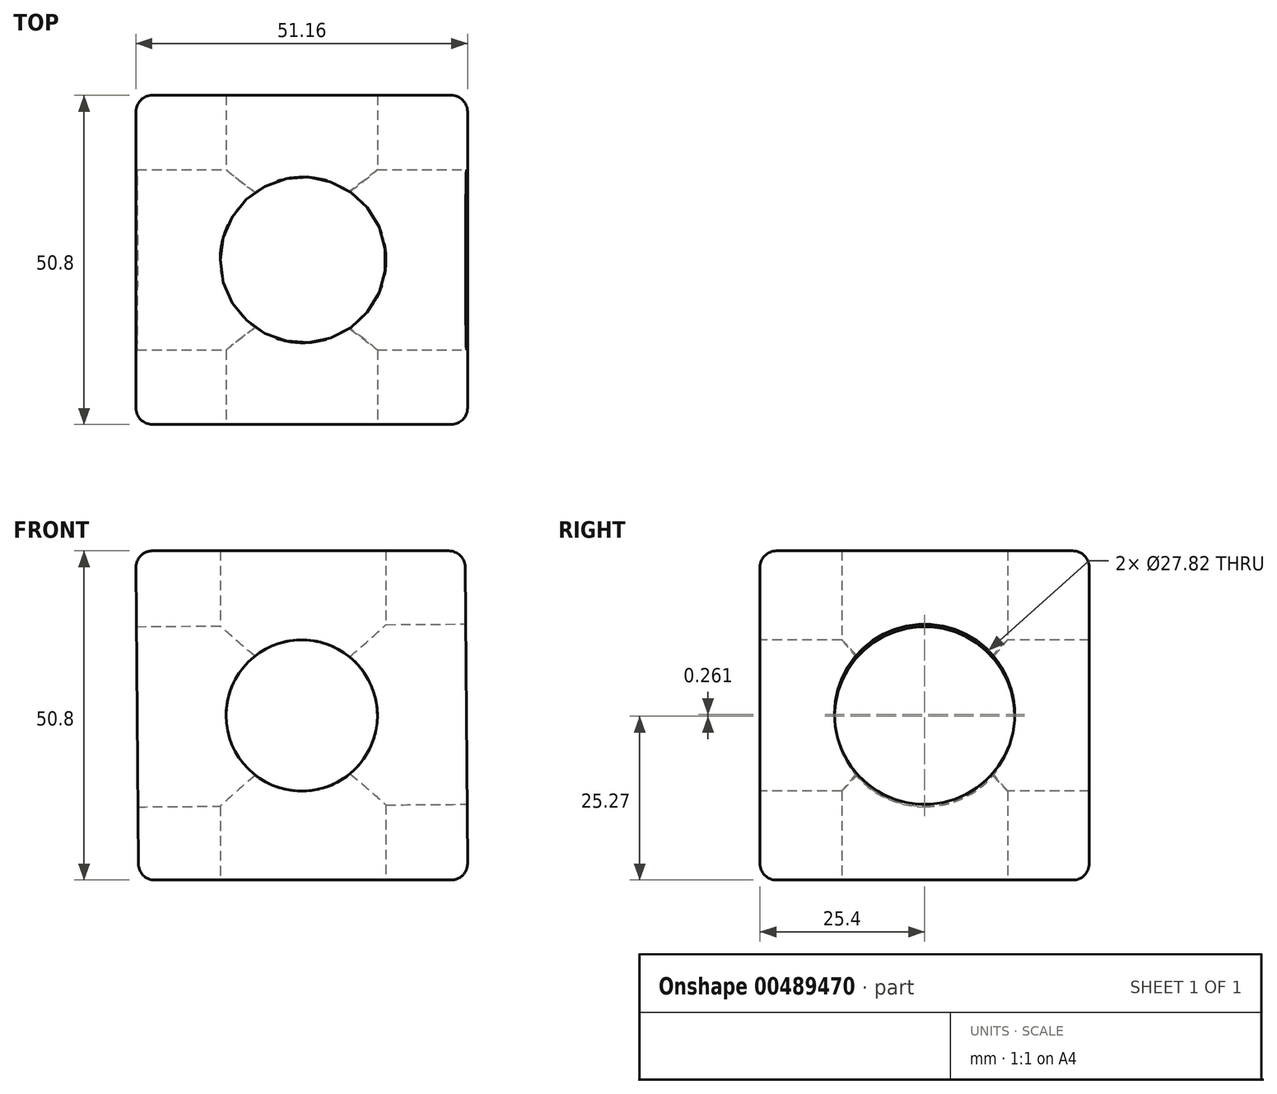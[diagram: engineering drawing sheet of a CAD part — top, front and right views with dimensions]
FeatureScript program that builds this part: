
annotation { "Feature Type Name" : "Feature", "Feature Type Description" : "" }
export const myFeature = defineFeature(function(context is Context, id is Id, definition is map)
    precondition{}
    {
        {
            var Q0;
            Q0=qCreatedBy(makeId("Front.planeOp"),FACE);
            var sketch = newSketch(context, id + "F0", { "sketchPlane" : qUnion([Q0])});
            skLineSegment(sketch, "E0", {"start": v(50.8, 0) * mm, "end": v(50.4, 50.8) * mm});
            skLineSegment(sketch, "E1", {"start": v(50.4, 50.8) * mm, "end": v(-0.4, 50.8) * mm});
            skLineSegment(sketch, "E2", {"start": v(0, 0) * mm, "end": v(50.8, 0) * mm});
            skLineSegment(sketch, "E3", {"start": v(-0.4, 50.8) * mm, "end": v(0, 0) * mm});
            skSolve(sketch);
        }
        {
            var Q0;
            Q0 = qSketchRegion(id + "F0", true);
            extrude(context, id + "F1", {"entities" : qUnion([Q0]), "depth" : 50.8 * mm});
        }
        {
            var Q0;
            Q0=makeQuery(id+"F1.opExtrude","CAP_FACE",FACE,{"disambiguationData":[OSD([sQuery(id+"F0.wireOp",EDGE,"E0"),sQuery(id+"F0.wireOp",EDGE,"E1"),sQuery(id+"F0.wireOp",EDGE,"E2"),sQuery(id+"F0.wireOp",EDGE,"E3")])],"isStart":false});
            var sketch = newSketch(context, id + "F2", { "sketchPlane" : qUnion([Q0])});
            skCircle(sketch, "E4", {"center": v(25.2, 25.4) * mm, "radius": 11.67 * mm});
            skPoint(sketch, "E5.orphan", {"position": v(-0.4, 50.8) * mm});
            skPoint(sketch, "E6.end.orphan", {"position": v(50.8, 0) * mm});
            skSolve(sketch);
        }
        {
            var Q0;
            Q0 = qSketchRegion(id + "F2", true);
            extrude(context, id + "F3", {"entities" : qUnion([Q0]), "operationType" : NewBodyOperationType.REMOVE, "oppositeDirection" : true, "depth" : 50.8 * mm});
        }
        {
            var Q0;
            Q0=makeQuery(id+"F1.opExtrude","SWEPT_FACE",FACE,{"disambiguationData":[OSD([sQuery(id+"F0.wireOp",EDGE,"E0")])]});
            var sketch = newSketch(context, id + "F4", { "sketchPlane" : qUnion([Q0])});
            skLineSegment(sketch, "E7", {"start": v(-25.4, 50.4) * mm, "end": v(-25.4, 0) * mm});
            skCircle(sketch, "E8", {"center": v(-25.4, 25.2) * mm, "radius": 13.91 * mm});
            skSolve(sketch);
        }
        {
            var Q0;
            Q0 = qSketchRegion(id + "F4", true);
            extrude(context, id + "F5", {"entities" : qUnion([Q0]), "operationType" : NewBodyOperationType.REMOVE, "oppositeDirection" : true, "depth" : 50.8 * mm});
        }
        {
            var Q0;
            Q0=makeQuery(id+"F1.opExtrude","SWEPT_FACE",FACE,{"disambiguationData":[OSD([sQuery(id+"F0.wireOp",EDGE,"E2")])]});
            var sketch = newSketch(context, id + "F6", { "sketchPlane" : qUnion([Q0])});
            skCircle(sketch, "E9", {"center": v(25.4, 25.4) * mm, "radius": 12.79 * mm});
            skSolve(sketch);
        }
        {
            var Q0;
            Q0 = qSketchRegion(id + "F6", true);
            extrude(context, id + "F7", {"entities" : qUnion([Q0]), "operationType" : NewBodyOperationType.REMOVE, "oppositeDirection" : true, "depth" : 50.8 * mm});
        }
        {
            var Q0;
            Q0=makeQuery(id+"F1.opExtrude","CAP_EDGE",EDGE,{"disambiguationData":[OSD([sQuery(id+"F0.wireOp",EDGE,"E0")])],"isStart":true});
            var Q1;
            Q1=makeQuery(id+"F1.opExtrude","SWEPT_EDGE",EDGE,{"disambiguationData":[OSD([sQuery(id+"F0.wireOp",EDGE,"E0"),sQuery(id+"F0.wireOp",EDGE,"E1")])]});
            var Q2;
            Q2=makeQuery(id+"F1.opExtrude","CAP_EDGE",EDGE,{"disambiguationData":[OSD([sQuery(id+"F0.wireOp",EDGE,"E0")])],"isStart":false});
            var Q3;
            Q3=makeQuery(id+"F1.opExtrude","SWEPT_EDGE",EDGE,{"disambiguationData":[OSD([sQuery(id+"F0.wireOp",EDGE,"E0"),sQuery(id+"F0.wireOp",EDGE,"E2")])]});
            var Q4;
            Q4=makeQuery(id+"F1.opExtrude","CAP_EDGE",EDGE,{"disambiguationData":[OSD([sQuery(id+"F0.wireOp",EDGE,"E1")])],"isStart":true});
            var Q5;
            Q5=makeQuery(id+"F1.opExtrude","CAP_EDGE",EDGE,{"disambiguationData":[OSD([sQuery(id+"F0.wireOp",EDGE,"E1")])],"isStart":false});
            var Q6;
            Q6=makeQuery(id+"F1.opExtrude","CAP_EDGE",EDGE,{"disambiguationData":[OSD([sQuery(id+"F0.wireOp",EDGE,"E2")])],"isStart":true});
            var Q7;
            Q7=makeQuery(id+"F1.opExtrude","CAP_EDGE",EDGE,{"disambiguationData":[OSD([sQuery(id+"F0.wireOp",EDGE,"E2")])],"isStart":false});
            var Q8;
            Q8=makeQuery(id+"F1.opExtrude","CAP_EDGE",EDGE,{"disambiguationData":[OSD([sQuery(id+"F0.wireOp",EDGE,"E3")])],"isStart":true});
            var Q9;
            Q9=makeQuery(id+"F1.opExtrude","SWEPT_EDGE",EDGE,{"disambiguationData":[OSD([sQuery(id+"F0.wireOp",EDGE,"E1"),sQuery(id+"F0.wireOp",EDGE,"E3")])]});
            var Q10;
            Q10=makeQuery(id+"F1.opExtrude","CAP_EDGE",EDGE,{"disambiguationData":[OSD([sQuery(id+"F0.wireOp",EDGE,"E3")])],"isStart":false});
            var Q11;
            Q11=makeQuery(id+"F1.opExtrude","SWEPT_EDGE",EDGE,{"disambiguationData":[OSD([sQuery(id+"F0.wireOp",EDGE,"E2"),sQuery(id+"F0.wireOp",EDGE,"E3")])]});
            var Q12;
            Q12=makeQuery(id+"F5.boolean.opBoolean","COPY",EDGE,{"derivedFrom":makeQuery(id+"F5.opExtrude","CAP_EDGE",EDGE,{"disambiguationData":[OSD([sQuery(id+"F4.wireOp",EDGE,"E8")])],"isStart":false})});
            var Q13;
            Q13=makeQuery(id+"F3.boolean.opBoolean","COPY",EDGE,{"derivedFrom":makeQuery(id+"F3.opExtrude","CAP_EDGE",EDGE,{"disambiguationData":[OSD([sQuery(id+"F2.wireOp",EDGE,"E4")])],"isStart":true})});
            var Q14;
            Q14=makeQuery(id+"F7.boolean.opBoolean","COPY",EDGE,{"derivedFrom":makeQuery(id+"F7.opExtrude","CAP_EDGE",EDGE,{"disambiguationData":[OSD([sQuery(id+"F6.wireOp",EDGE,"E9")])],"isStart":true})});
            var Q15;
            Q15=makeQuery(id+"F7.boolean.opBoolean","COPY",EDGE,{"derivedFrom":makeQuery(id+"F7.opExtrude","CAP_EDGE",EDGE,{"disambiguationData":[OSD([sQuery(id+"F6.wireOp",EDGE,"E9")])],"isStart":false})});
            var Q16;
            Q16=makeQuery(id+"F5.boolean.opBoolean","COPY",EDGE,{"derivedFrom":makeQuery(id+"F5.opExtrude","CAP_EDGE",EDGE,{"disambiguationData":[OSD([sQuery(id+"F4.wireOp",EDGE,"E8")])],"isStart":true})});
            var Q17;
            Q17=makeQuery(id+"F3.boolean.opBoolean","COPY",EDGE,{"derivedFrom":makeQuery(id+"F3.opExtrude","CAP_EDGE",EDGE,{"disambiguationData":[OSD([sQuery(id+"F2.wireOp",EDGE,"E4")])],"isStart":false})});
            fillet(context, id + "F8", {"entities" : qUnion([Q0, Q1, Q2, Q3, Q4, Q5, Q6, Q7, Q8, Q9, Q10, Q11, Q12, Q13, Q14, Q15, Q16, Q17]), "radius" : 2.54 * mm, "tangentPropagation" : true, "allowEdgeOverflow" : false});
        }
    });
